# Revit family: Faucet-Bath_Filler-KOHLER-Laminar-K-922
name_source: partatom
category: Plumbing Fixtures
revit_build: Autodesk Revit 2015 (Build: 20140606_1530(x64)
units: mm (PartAtom-declared; Revit-internal decimal feet)

## types (3) — shared parameters
ADA Compliant = No
Assembly Code = D2010
CW Connection = No
Cold Water Inlet = Cold Water Inlet
Date Modified = 12/18/2018
Default Elevation = 36"
Description = Laminar wall- or ceiling-mount bath filler with 0.8 inch orifice
Drain Included = No
Faucet Hole Spacing = 0"
Flow Rate = 0 GPM
HW Connection = Yes
Handle Clearance = 0"
Height = 4 1/4"
Hot Water Inlet = Tempered Water Inlet
Length = 5/8"
Manufacturer = KOHLER Co.
MasterFormat 1995 = 15410
MasterFormat 2004 = 22.41.39
Material = Solid Brass Construction
Pressure = 0.00 psi
Product Documentation Link = http://www.us.kohler.com
Product Name = Laminar
Product Page URL = http://www.us.kohler.com
Spout Reach = 0"
URL = https://www.us.kohler.com
Vent Connection = No
Waste Connection = No
Waste Water Outlet = Waste Water Outlet
Width = 4 1/4"

## per-type parameters (varying)
| type | Finish | Model | Type |
| CP-Polished Chrome | Kohler-Metal-CP-Polished_Chrome | K-922-CP | 1 |
| AF-Vibrant French Gold | Kohler-Metal-AF-Vibrant_French_Gold | K-922-AF | 2 |
| BN-Vibrant Brushed Nickel | Kohler-Metal-BN-Vibrant_Brushed_Nickel | K-922-BN | 3 |

## geometry (parser evidence)
native form markers: Sweep x6
no freeform markers — native parametric forms only
